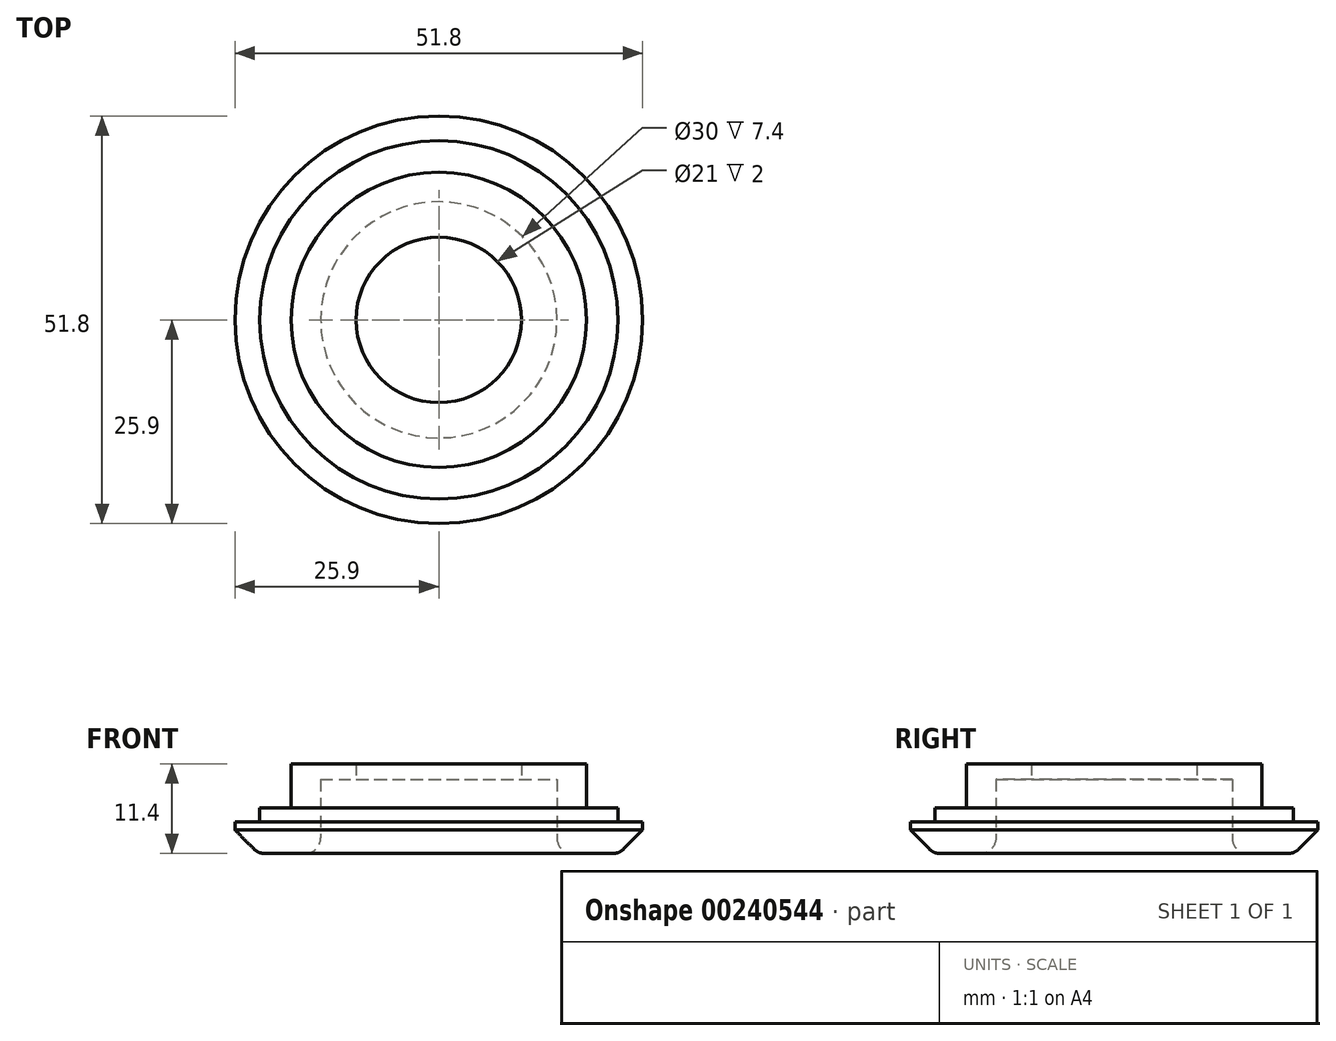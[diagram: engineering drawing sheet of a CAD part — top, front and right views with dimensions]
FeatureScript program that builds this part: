
annotation { "Feature Type Name" : "Feature", "Feature Type Description" : "" }
export const myFeature = defineFeature(function(context is Context, id is Id, definition is map)
    precondition{}
    {
        {
            var Q0;
            Q0=qCreatedBy(makeId("Front.planeOp"),FACE);
            var sketch = newSketch(context, id + "F0", { "sketchPlane" : qUnion([Q0])});
            skLineSegment(sketch, "E0", {"start": v(-17, 0) * mm, "end": v(-22.07, 0) * mm});
            skLineSegment(sketch, "E1", {"start": v(-25.9, 3) * mm, "end": v(-25.9, 4) * mm});
            skLineSegment(sketch, "E2", {"start": v(-25.9, 4) * mm, "end": v(-22.75, 4) * mm});
            skLineSegment(sketch, "E3", {"start": v(-22.75, 4) * mm, "end": v(-22.75, 5.8) * mm});
            skLineSegment(sketch, "E4", {"start": v(-22.75, 5.8) * mm, "end": v(-18.75, 5.8) * mm});
            skLineSegment(sketch, "E5", {"start": v(-18.75, 5.8) * mm, "end": v(-18.75, 11.4) * mm});
            skLineSegment(sketch, "E6", {"start": v(-18.75, 11.4) * mm, "end": v(-10.5, 11.4) * mm});
            skLineSegment(sketch, "E7", {"start": v(-10.5, 11.4) * mm, "end": v(-10.5, 9.4) * mm});
            skLineSegment(sketch, "E8", {"start": v(-10.5, 9.4) * mm, "end": v(-15, 9.4) * mm});
            skLineSegment(sketch, "E9", {"start": v(-15, 9.4) * mm, "end": v(-15, 2) * mm});
            skLineSegment(sketch, "E10", {"start": v(0, 0) * mm, "end": v(0, 11.4) * mm, "construction": true});
            skLineSegment(sketch, "E11", {"start": v(-25.9, 3) * mm, "end": v(-23.49, 0.59) * mm});
            skPoint(sketch, "E12.visualSharp", {"position": v(-15, 0) * mm});
            skArc(sketch, "E12.filletArc", {"start": v(-17, 0) * mm, "mid": v(-15.59, 0.59) * mm, "end": v(-15, 2) * mm});
            skPoint(sketch, "E13.visualSharp", {"position": v(-22.9, 0) * mm});
            skArc(sketch, "E13.filletArc", {"start": v(-23.49, 0.59) * mm, "mid": v(-22.84, 0.15) * mm, "end": v(-22.07, 0) * mm});
            skSolve(sketch);
        }
        {
            var Q0;
            Q0 = qSketchRegion(id + "F0", true);
            var Q1;
            Q1=sQuery(id+"F0.wireOp",EDGE,"E10");
            revolve(context, id + "F1", {"entities" : qUnion([Q0]), "axis" : qUnion([Q1]), "revolveType" : RevolveType.FULL});
        }
    });
